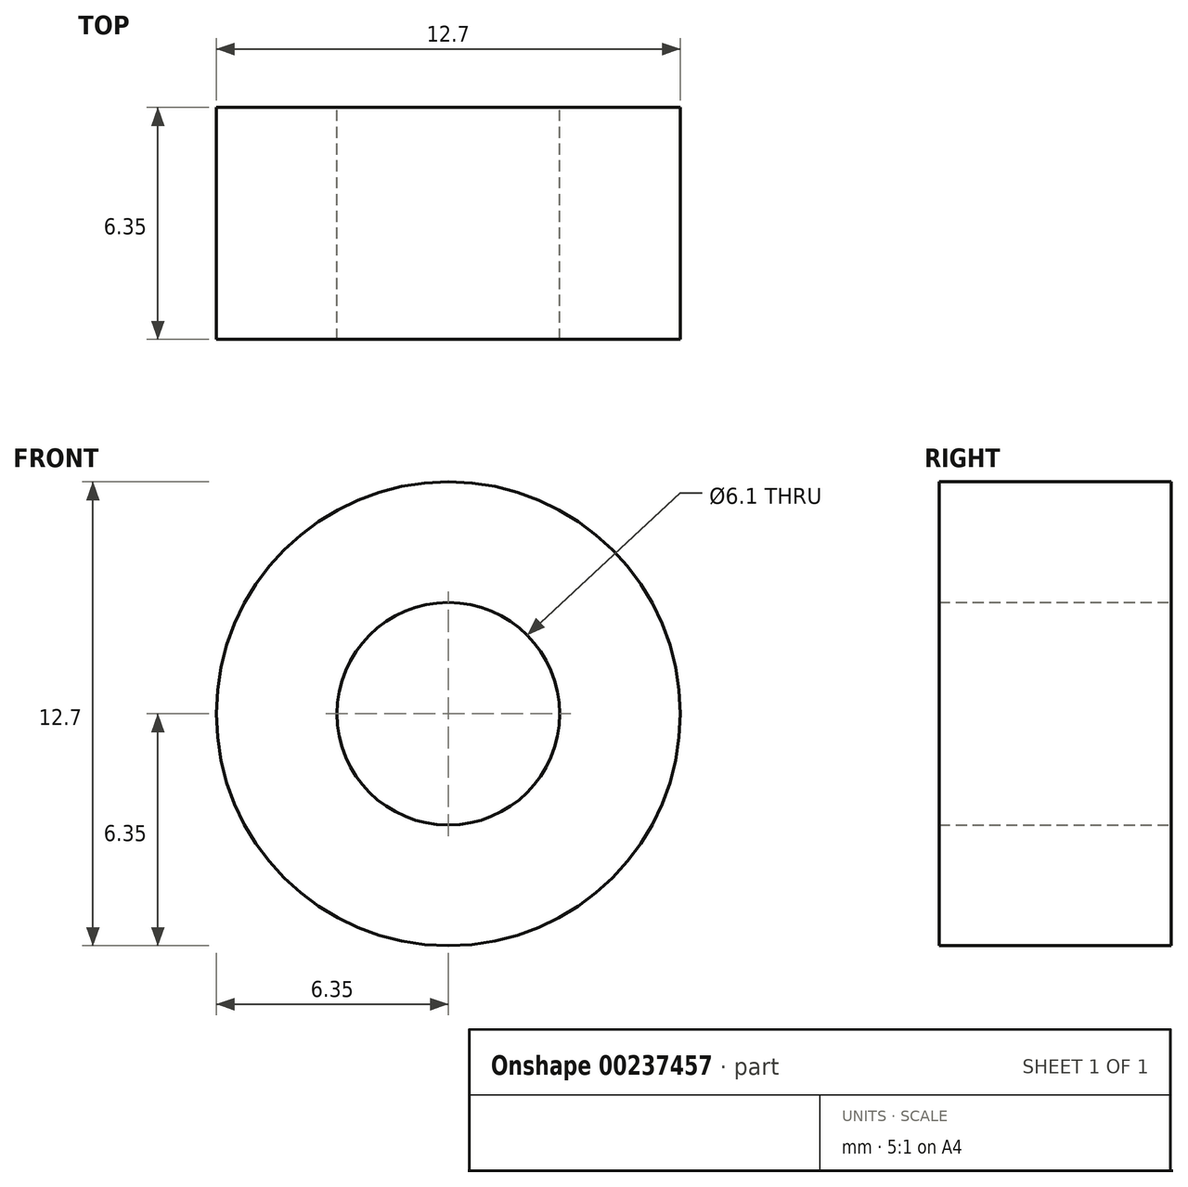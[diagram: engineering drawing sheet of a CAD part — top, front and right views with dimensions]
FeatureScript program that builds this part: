
annotation { "Feature Type Name" : "Feature", "Feature Type Description" : "" }
export const myFeature = defineFeature(function(context is Context, id is Id, definition is map)
    precondition{}
    {
        {
            var Q0;
            Q0=qCreatedBy(makeId("Front.planeOp"),FACE);
            var sketch = newSketch(context, id + "F0", { "sketchPlane" : qUnion([Q0])});
            skCircle(sketch, "E0", {"center": v(0, 0) * mm, "radius": 6.35 * mm});
            skCircle(sketch, "E1", {"center": v(0, 0) * mm, "radius": 3.05 * mm});
            skSolve(sketch);
        }
        {
            var Q0;
            Q0=makeQuery(id+"F0.imprint","IMPRINT",FACE,{"disambiguationData":[TD([[makeQuery(id+"F0.imprint","IMPRINT",EDGE,{"derivedFrom":sQuery(id+"F0.wireOp",EDGE,"E0")}),1.0]])]});
            extrude(context, id + "F1", {"entities" : qUnion([Q0]), "depth" : 6.35 * mm});
        }
    });
